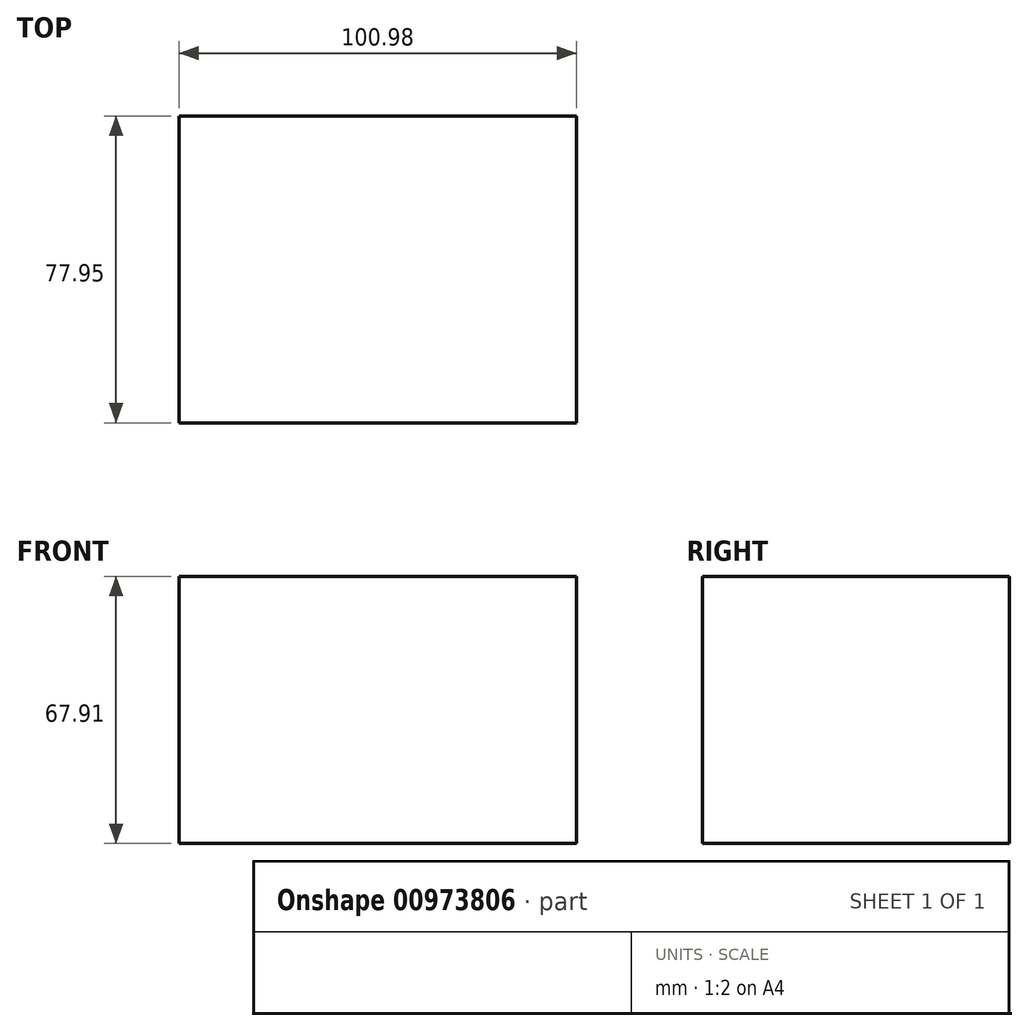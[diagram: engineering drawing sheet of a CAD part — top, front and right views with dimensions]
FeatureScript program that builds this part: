
annotation { "Feature Type Name" : "Feature", "Feature Type Description" : "" }
export const myFeature = defineFeature(function(context is Context, id is Id, definition is map)
    precondition{}
    {
        {
            var Q0;
            Q0=qCreatedBy(makeId("Top.planeOp"),FACE);
            var sketch = newSketch(context, id + "F0", { "sketchPlane" : qUnion([Q0])});
            skLineSegment(sketch, "E0.bottom", {"start": v(-34.85, 37.12) * mm, "end": v(66.13, 37.12) * mm});
            skLineSegment(sketch, "E0.top", {"start": v(-34.85, -40.83) * mm, "end": v(66.13, -40.83) * mm});
            skLineSegment(sketch, "E0.left", {"start": v(-34.85, 37.12) * mm, "end": v(-34.85, -40.83) * mm});
            skLineSegment(sketch, "E0.right", {"start": v(66.13, 37.12) * mm, "end": v(66.13, -40.83) * mm});
            skSolve(sketch);
        }
        {
            var Q0;
            Q0=makeQuery(id+"F0.imprint","IMPRINT",FACE,{"disambiguationData":[TD([[makeQuery(id+"F0.imprint","IMPRINT",EDGE,{"derivedFrom":sQuery(id+"F0.wireOp",EDGE,"E0.bottom")}),-1.0]])]});
            extrude(context, id + "F1", {"entities" : qUnion([Q0]), "depth" : 67.9 * mm, "offsetDistance" : 25.4 * mm});
        }
    });
